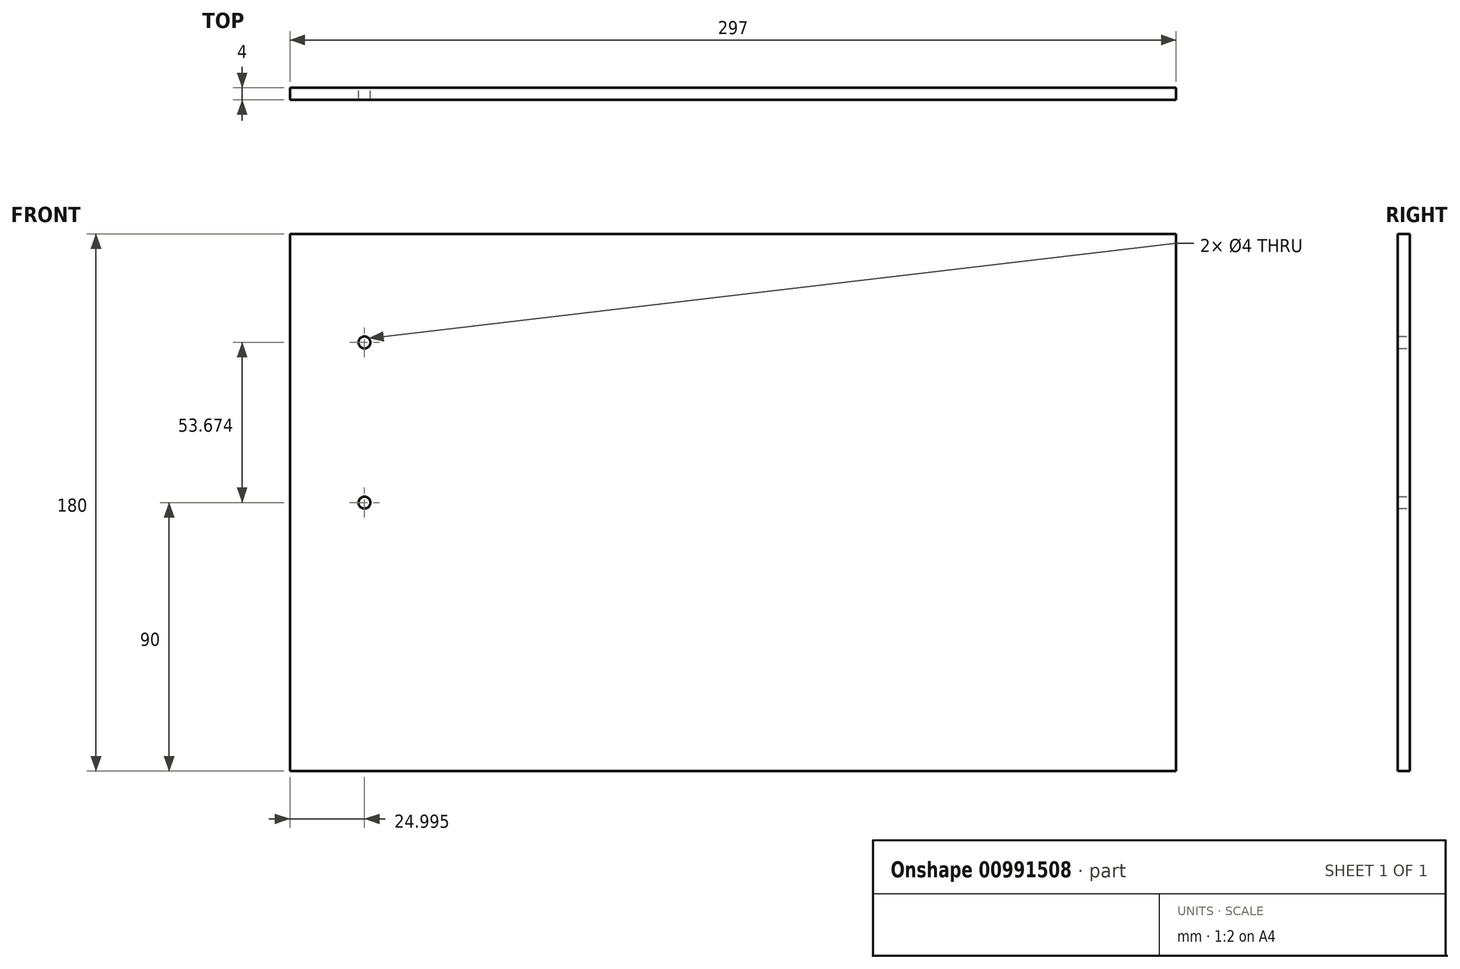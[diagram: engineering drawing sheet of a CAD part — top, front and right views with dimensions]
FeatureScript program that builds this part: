
annotation { "Feature Type Name" : "Feature", "Feature Type Description" : "" }
export const myFeature = defineFeature(function(context is Context, id is Id, definition is map)
    precondition{}
    {
        {
            var Q0;
            Q0=qCreatedBy(makeId("Front.planeOp"),FACE);
            var sketch = newSketch(context, id + "F0", { "sketchPlane" : qUnion([Q0])});
            skLineSegment(sketch, "E0.bottom", {"start": v(-115.51, 90) * mm, "end": v(181.49, 90) * mm});
            skLineSegment(sketch, "E0.top", {"start": v(-115.51, -90) * mm, "end": v(181.49, -90) * mm});
            skLineSegment(sketch, "E0.left", {"start": v(-115.51, 90) * mm, "end": v(-115.51, -90) * mm});
            skLineSegment(sketch, "E0.right", {"start": v(181.49, 90) * mm, "end": v(181.49, -90) * mm});
            skPoint(sketch, "E0.middle", {"position": v(32.99, 0) * mm});
            skCircle(sketch, "E1", {"center": v(-90.51, 53.67) * mm, "radius": 2 * mm});
            skCircle(sketch, "E2", {"center": v(-90.51, 0) * mm, "radius": 2 * mm});
            skSolve(sketch);
        }
        {
            var Q0;
            Q0 = qSketchRegion(id + "F0", true);
            extrude(context, id + "F1", {"entities" : qUnion([Q0]), "depth" : 4 * mm, "offsetDistance" : 25 * mm});
        }
    });
